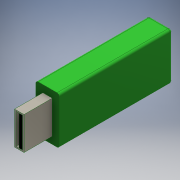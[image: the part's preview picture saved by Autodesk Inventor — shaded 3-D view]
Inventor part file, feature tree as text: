
AUTODESK INVENTOR PART (.ipt)
format: ipt  version: 2016 (Build 200138000, 138)  size: 172,032 bytes
history: native  units: mm
features: extrude x5, sketch x5, projected_geometry x4, fillet x1
ambient origin geometry x8: Origin, YZ Plane, XZ Plane, XY Plane, X Axis, Y Axis, Z Axis, Center Point
bodies: Solid1 (feature_tree)
feature tree (15):
  extrude  "Extrusion1"  Depth=25.0mm
  extrude  "Extrusion2"  Depth=10.0mm
  extrude  "Extrusion3"  Depth=1.5mm
  extrude  "Extrusion4"  Depth=30.0mm TaperAngle=0.0deg
  fillet  "Fillet1"  Radius=6.5mm
  extrude  "Extrusion5"  Depth=8.0mm
  sketch  "Sketch1"  dims[d0=50.0mm d1=25.0mm]
  sketch  "Sketch2"  dims[d2=120.0mm d3=0.0mm d4=10.0mm]
  projected_geometry  "Projected Loop1"
  sketch  "Sketch3"  dims[d5=30.0mm d6=0.0mm d7=1.5mm]
  projected_geometry  "Projected Loop2"
  sketch  "Sketch4"  dims[d8=1.5mm d9=30.0mm d10=0.0mm d11=6.5mm]
  projected_geometry  "Projected Loop3"
  sketch  "Sketch5"  dims[d12=6.0mm d13=8.0mm d14=1.0mm d15=0.0mm d16=2.5mm d17=1.5mm d18=1.5mm d19=0.01mm d20=0.0mm]
  projected_geometry  "Projected Loop4"
